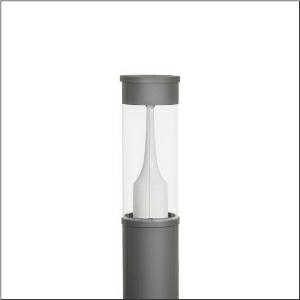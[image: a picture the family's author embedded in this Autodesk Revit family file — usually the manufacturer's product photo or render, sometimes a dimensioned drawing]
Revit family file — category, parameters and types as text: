
# Revit family: city-light_120_iq___p1_0a_5xa5285nf14h_00f5
name_source: partatom
category: Lighting Fixtures
units: mm (PartAtom-declared; Revit-internal decimal feet)

## family parameters
Cut with Voids When Loaded = No
Host = Face
Light Source = No
Part Type = Normal
Room Calculation Point = No
Round Connector Dimension = Use Diameter
Shared = No

## types (1)
- --- (1 x LED, 1510 lm, 11.8 W, 2700K)
    Apparent Load = 12 VA
    CIE Flux Codes = 32 61 90 93 100
    Color Rendering = 70
    Color Temperature = 2700K
    Default Elevation = 1800 mm
    Description = City-Light 120 iQ, bollard luminaire, Module 540 iQ-SR, primary light control with 3 zone facetted reflector, of plastic, silver coated, highly specular, structured, primary optical cover: cover, of PMMA, transparent, partly coated, light distribution: P1.0a, primary light characteristic: strongly asymmetric, LED, High Power LED, rated luminous flux: 1.510lm, luminous efficacy: 128lm/W, light colour: 727, colour temperature: 2700K, control gear: iQ Street-Remote, control: pre-setting: logarithmic dimming characteristic, Street-Remote, Auto-Match, Temp-Guard, Lumen-Switch, Night-Set, Smart-Wire, Light-Fading, Desk-Remote (wireless, voltage-free reading and setting of iQ features in the workshop via application-optimized NFC function/RFID function), optimised constant luminous flux control (CLO 2.0), with terminal, 6-pole, max. 2.5mm², mains connection: 230..240V, AC, 50/60Hz, start of lifetime: 12W, end of service life: 12W, reduction: 6W, luminaire housing, cylindrical, of extruded aluminium section, coated, Siteco® metallic grey (DB 702S), length: 1.200mm, diameter: 200mm, Module 540 iQ-SR, traffic white (RAL 9016), equipment: standard, protection rating (complete): IP54, insulation class (complete): insulation class II (safety insulation), certification: CE, ENEC, VDE, packaging unit: 1 piece

Light Distribution: P1.0a
    Height = 500 mm
    Lamp = 1 x LED
    Lamp Light Flux = 1510 lm
    Lamp Power = 11.8 W
    Lamp count = 1
    Length = 200 mm  [stored 0.656168 ft]
    Luminous efficacy = 128 lm/W
    Manufacturer = Siteco
    ModVariant = No
    Model = 5XA5285NF14H
    Mounting Place = Floor
    Mounting Type = Freestanding
    Number of Poles = 1
    OnlyDefault = Yes
    Power Factor = 1
    Product Name = City-Light 120 iQ | P1.0a
    Product group = bollard luminaire
    ProductGroupID = 1304
    Protection Class = Protection class II
    Protection Degree = IP 54
    RLX_Detail_Level = 1
    RLX_Emergency_Light_Flux = 0 lm
    RLX_Emergency_Type = 0
    RLX_Emergency_Type_DB = No
    RlxData = <blob elided: 52421 chars, md5=86e13314>
    Socket = socket
    Standby Power = 0 W
    System Light Flux = 1510 lm
    System Power = 12 W
    Type Comments = factory setting: luminous flux: 100 % | dim-lin: 254 | 472 mA
    Type Image = l_1006922.jpg
    URL = http://relux.com
    VarID = @adj_152675
    Voltage = 0 V
    Weight = 0.00 kg
    Width = 0 mm  [stored 0 ft]

note: [stored X ft] marks values corroborated as IEEE doubles in the binary element streams (Revit-internal decimal feet)

## geometry (parser evidence)
native form markers: Blend x4, Sweep x12
no freeform markers — native parametric forms only
